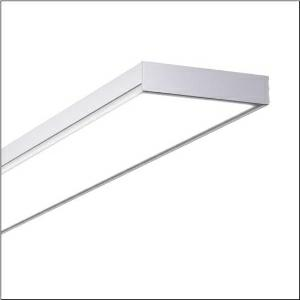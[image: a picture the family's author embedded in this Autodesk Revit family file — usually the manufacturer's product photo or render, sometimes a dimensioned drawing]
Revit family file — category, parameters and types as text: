
# Revit family: apollon_31_surface_51mp25wm2441ea
name_source: partatom
category: Lighting Fixtures
units: mm (PartAtom-declared; Revit-internal decimal feet)

## family parameters
Cut with Voids When Loaded = No
Host = Face
Light Source = No
Part Type = Normal
Room Calculation Point = No
Round Connector Dimension = Use Diameter
Shared = No

## types (1)
- Apollon 31 Surface (1 x LED, 3800 lm, 27 W, 4000K)
    Apparent Load = 27 VA
    CIE Flux Codes = 61 87 97 97 100
    Color Rendering = 80
    Color Temperature = 4000K
    Default Elevation = 1800 mm
    Description = Apollon 31 Surface, office luminaire, primary optical cover: micro prismatic cover, of PMMA, light emission: direct distribution, primary light characteristic: symmetric, installation type: surface-mounted, LED, rated luminous flux: 3.800lm, luminous efficacy: 139lm/W, light colour: 840, colour temperature: 4000K, control gear: ON/OFF Multilumen, with terminal, 3-pole, mains connection: 220..240V, AC, 50/60Hz, rated input power: 27W, housing, of sheet steel, coated, metallic grey (RAL 9006), length: 1.245mm, width: 200mm, height: 44mm, protection rating (complete): IP20, protection rating (on room side): IP40, protection rating (lamp compartment, on room side): IP40, insulation class (complete): insulation class I (protective earthing), certification: CE, ENEC, UKCA, impact resistance: IK02, permissible operating ambient temperature: -20..+40°C, packaging unit: 1 piece
    Height = 44 mm
    Lamp = 1 x LED
    Lamp Light Flux = 3800 lm
    Lamp Power = 27 W
    Lamp count = 1
    Length = 1245 mm
    Luminous efficacy = 141 lm/W
    Manufacturer = Siteco
    ModVariant = No
    Model = 51MP25WM2441EA
    Mounting Place = Ceiling
    Mounting Type = Surface mounted
    Number of Poles = 1
    OnlyDefault = Yes
    Power Factor = 1
    Product Name = Apollon 31 Surface
    Product group = office luminaire | ceiling mounted
    ProductGroupID = 301
    Protection Class = Protection class I
    Protection Degree = IP 20
    RLX_Detail_Level = 1
    RLX_Emergency_Light_Flux = 0 lm
    RLX_Emergency_Type = 0
    RLX_Emergency_Type_DB = No
    RlxData = <blob elided: 24121 chars, md5=91b2c5ed>
    Socket = socket
    Standby Power = 0 W
    System Light Flux = 3800 lm
    System Power = 27 W
    Type Comments = Product without accessories
    Type Image = l_1313654.jpg
    URL = http://relux.com
    VarID = ---
    Voltage = 0 V
    Weight = 0.00 kg
    Width = 200 mm  [stored 0.656168 ft]

note: [stored X ft] marks values corroborated as IEEE doubles in the binary element streams (Revit-internal decimal feet)

## geometry (parser evidence)
native form markers: Blend x4, Sweep x10
no freeform markers — native parametric forms only
